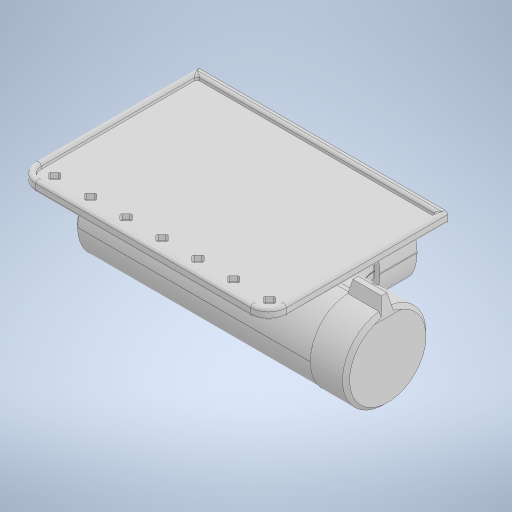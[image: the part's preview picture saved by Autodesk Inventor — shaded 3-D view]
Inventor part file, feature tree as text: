
AUTODESK INVENTOR PART (.ipt)
format: ipt  version: 2024.1 (Build 281209000, 209)  size: 670,208 bytes
history: native  units: mm
features: fillet x12, extrude x8, sketch x8, chamfer x5, projected_geometry x4, plane x1, other x1
ambient origin geometry x8: Origin, YZ Plane, XZ Plane, XY Plane, X Axis, Y Axis, Z Axis, Center Point
bodies: Solid1 (feature_tree)
feature tree (39):
  extrude  "Extrusion1"  Depth=36.0mm
  fillet  "Fillet1"  Radius=46.7mm
  fillet  "Fillet2"  Radius=26.0mm
  fillet  "Fillet3"  Radius=26.0mm
  extrude  "Extrusion2"  Depth=44.56mm TaperAngle=0.0deg
  extrude  "Extrusion3"  Depth=22.25mm
  chamfer  "Chamfer1"  Distance=20.0mm
  chamfer  "Chamfer2"  Distance=3.0mm
  chamfer  "Chamfer3"  Distance=3.0mm
  chamfer  "Chamfer4"  Distance=1.5mm
  extrude  "Extrusion4"  Depth=10.0mm TaperAngle=0.0deg
  extrude  "Extrusion5"  Depth=10.0mm TaperAngle=45.0deg
  fillet  "Fillet4"  Radius=10.0mm
  fillet  "Fillet5"  Radius=10.0mm
  extrude  "Extrusion6"  Depth=10.0mm TaperAngle=45.0deg
  fillet  "Fillet6"  Radius=60.0mm
  fillet  "Fillet7"  Radius=80.0mm
  fillet  "Fillet8"  Radius=100.0mm
  fillet  "Fillet9"  Radius=3.0mm
  plane  "Work Plane1"
  extrude  "Extrusion7"  Depth=3.0mm
  fillet  "Fillet10"  Radius=35.0mm
  fillet  "Fillet11"  Radius=20.75mm
  extrude  "Extrusion8"  Depth=10.0mm
  chamfer  "Chamfer5"  Distance=10.0mm
  fillet  "Fillet12"  Radius=3.0mm
  sketch  "Sketch1"  dims[d0=80.0mm d1=36.0mm d2=46.7mm d3=26.0mm d4=26.0mm]
  sketch  "Sketch2"  dims[d5=132.0mm d6=44.56mm d7=0.0mm]
  sketch  "Sketch3"  dims[d8=22.0mm d9=22.25mm]
  sketch  "Sketch4"  dims[d10=15.0mm]
  other  "TRAY"
  sketch  "Sketch5"  dims[d11=46.7mm]
  projected_geometry  "Projected Loop1"
  sketch  "Sketch6"  dims[d12=44.56mm]
  projected_geometry  "Projected Loop2"
  sketch  "Sketch7"  dims[d13=22.28mm d14=20.0mm d15=0.0mm]
  projected_geometry  "Projected Loop3"
  projected_geometry  "Projected Loop4"
  sketch  "Sketch8"  dims[d16=30.0mm d17=3.0mm d18=3.0mm d19=1.5mm d20=20.0mm d21=0.0mm d22=2.0mm d23=2.0mm d24=45.0deg d25=10.0mm d26=2.0mm d27=45.0deg d28=10.0mm d29=2.0mm d30=45.0deg d31=2.0mm d32=2.0mm d33=45.0deg d34=60.0mm d35=80.0mm d36=100.0mm d37=3.0mm d38=0.0mm d39=3.0mm d40=35.0mm d41=20.75mm d42=0.0mm d43=5.0mm d44=10.0mm d45=3.0mm d46=3.0mm d47=0.0mm d48=1.5mm d49=1.5mm d50=1.5mm d51=1.5mm d52=3.0mm d54=18.0mm d55=100.0mm d56=0.0mm d57=5.0mm d58=5.0mm d59=7.0mm d60=7.0mm d61=3.5mm d62=4.0mm d63=0.0mm d64=0.0mm d65=3.5mm d66=2.0mm d67=45.0deg d68=1.0mm d69=70.0mm d71=20.0mm d72=10.0mm d74=10.0mm d76=3.5mm]
